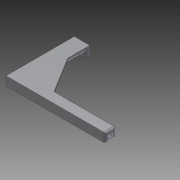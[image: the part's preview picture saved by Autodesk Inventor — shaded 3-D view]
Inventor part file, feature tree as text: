
AUTODESK INVENTOR PART (.ipt)
format: ipt  version: 2011 (Build 150239000, 239)  size: 103,936 bytes
history: native  units: mm
features: other x4, sketch x2
ambient origin geometry x8: Origin, YZ Plane, XZ Plane, XY Plane, X Axis, Y Axis, Z Axis, Center Point
feature tree (6):
  other  "Tirador.ipt"
  other  "Sólido1::Tirador.ipt"
  sketch  "Boceto1"  dims[d0=10.0mm]
  sketch  "Boceto2"
  other  "OperaciónIdentificador1"
  other  "Sólido1"
